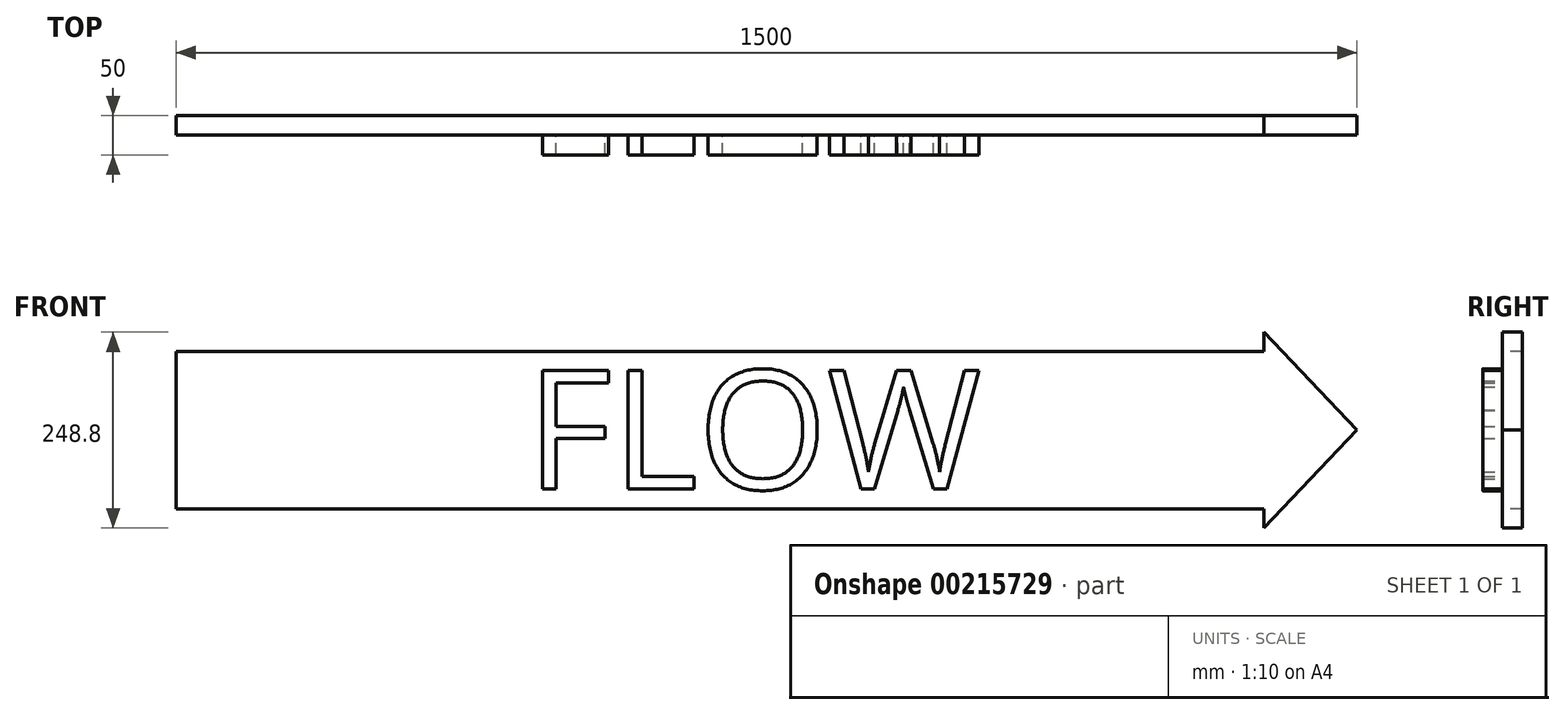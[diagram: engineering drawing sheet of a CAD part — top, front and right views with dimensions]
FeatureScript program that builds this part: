
annotation { "Feature Type Name" : "Feature", "Feature Type Description" : "" }
export const myFeature = defineFeature(function(context is Context, id is Id, definition is map)
    precondition{}
    {
        {
            var Q0;
            Q0=qCreatedBy(makeId("Front.planeOp"),FACE);
            var sketch = newSketch(context, id + "F0", { "sketchPlane" : qUnion([Q0])});
            skLineSegment(sketch, "E0", {"start": v(0, 0) * mm, "end": v(0, 100) * mm});
            skLineSegment(sketch, "E1", {"start": v(0, 100) * mm, "end": v(1381.62, 100) * mm});
            skLineSegment(sketch, "E2", {"start": v(1381.62, 100) * mm, "end": v(1381.62, 124.4) * mm});
            skLineSegment(sketch, "E3", {"start": v(1381.62, 124.4) * mm, "end": v(1500, 0) * mm});
            skLineSegment(sketch, "E4", {"start": v(1500, 0) * mm, "end": v(0, 0) * mm});
            skLineSegment(sketch, "E5.MirrorCS", {"start": v(0, 0) * mm, "end": v(0, -100) * mm});
            skLineSegment(sketch, "E6.MirrorCS", {"start": v(0, -100) * mm, "end": v(1381.62, -100) * mm});
            skLineSegment(sketch, "E7.MirrorCS", {"start": v(1381.62, -100) * mm, "end": v(1381.62, -124.4) * mm});
            skLineSegment(sketch, "E8.MirrorCS", {"start": v(1381.62, -124.4) * mm, "end": v(1500, 0) * mm});
            skSolve(sketch);
        }
        {
            var Q0;
            Q0 = qSketchRegion(id + "F0", true);
            extrude(context, id + "F1", {"entities" : qUnion([Q0]), "oppositeDirection" : true, "depth" : 25 * mm});
        }
        {
            var Q0;
            Q0=qCreatedBy(makeId("Front.planeOp"),FACE);
            var sketch = newSketch(context, id + "F2", { "sketchPlane" : qUnion([Q0])});
            skText(sketch, "E9", { "text": "FLOW", "fontName": "OpenSans-Regular.ttf"});
            const initialGuessF2  = {"E9": [0.4446, -0.07517, 1, 0, 0.15191]};
            skSetInitialGuess(sketch, initialGuessF2);
            skSolve(sketch);
        }
        {
            var Q0;
            Q0 = qSketchRegion(id + "F2", true);
            extrude(context, id + "F3", {"entities" : qUnion([Q0]), "operationType" : NewBodyOperationType.ADD, "depth" : 25 * mm});
        }
    });
